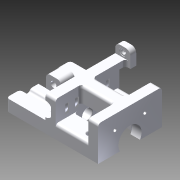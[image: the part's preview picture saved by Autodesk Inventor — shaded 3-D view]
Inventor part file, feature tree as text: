
AUTODESK INVENTOR PART (.ipt)
format: ipt  version: 2015 SP1 (Build 190203100, 203)  size: 731,136 bytes
history: native  units: mm
features: sketch x30, extrude x26, fillet x15, projected_geometry x14, reference x8, hole x4, mirror x1, plane x1, other x1, revolve x1
ambient origin geometry x8: Origin, YZ Plane, XZ Plane, XY Plane, X Axis, Y Axis, Z Axis, Center Point
bodies: Solid1 (feature_tree)
feature tree (101):
  extrude  "Extrusion1"  Depth=12.0mm
  extrude  "Extrusion2"  Depth=10.0mm
  extrude  "Extrusion3"  Depth=25.0mm TaperAngle=0.0deg
  extrude  "Extrusion4"  Depth=16.0mm TaperAngle=0.0deg
  extrude  "Extrusion5"  Depth=24.0mm TaperAngle=0.0deg
  extrude  "Extrusion6"  Depth=2.0mm
  extrude  "Extrusion7"  Depth=4.0mm
  mirror  "Mirror1"
  plane  "Work Plane1"
  extrude  "Extrusion9"  Depth=4.0mm
  sketch  "Sketch8"  dims[d19=4.0mm d20=4.0mm]
  other  "Work Axis1"
  revolve  "Revolution1"  [1 undecoded]
  fillet  "Fillet9"  Radius=2.0mm
  fillet  "Fillet11"  Radius=1.75mm
  extrude  "Extrusion18"  Depth=10.0mm TaperAngle=0.0deg
  extrude  "Extrusion19"  Depth=1.75mm
  extrude  "Extrusion20"  Depth=10.0mm TaperAngle=0.0deg
  fillet  "Fillet13"  Radius=5.0mm
  fillet  "Fillet12"  Radius=5.0mm
  extrude  "Extrusion21"  Depth=1.5mm
  extrude  "Extrusion22"  Depth=10.0mm
  extrude  "Extrusion23"  Depth=22.2mm
  fillet  "Fillet15"  Radius=8.0mm
  fillet  "Fillet16"  Radius=10.5mm
  fillet  "Fillet17"  Radius=8.0mm
  fillet  "Fillet18"  Radius=2.0mm
  hole  "Hole1"  [1 undecoded]
  extrude  "Extrusion25"  Depth=15.5mm
  extrude  "Extrusion26"  Depth=3.0mm TaperAngle=0.0deg
  fillet  "Fillet19"  Radius=2.0mm
  fillet  "Fillet20"  Radius=3.0mm
  hole  "Hole2"  [1 undecoded]
  hole  "Hole3"  [1 undecoded]
  fillet  "Fillet21"  Radius=19.0mm
  extrude  "Extrusion27"  Depth=14.0mm
  extrude  "Extrusion28"  Depth=16.0mm
  fillet  "Fillet23"  Radius=14.0mm
  extrude  "Extrusion29"  Depth=10.0mm TaperAngle=0.0deg
  extrude  "Extrusion30"  Depth=3.0mm
  hole  "Hole4"  [1 undecoded]
  extrude  "Extrusion31"  Depth=3.0mm
  fillet  "Fillet24"  Radius=4.5mm
  fillet  "Fillet25"  Radius=6.3515mm
  extrude  "Extrusion32"  Depth=3.0mm
  extrude  "Extrusion33"  TaperAngle=0.0deg  [1 undecoded]
  extrude  "Extrusion34"  Depth=10.0mm TaperAngle=0.0deg
  fillet  "Fillet26"  Radius=4.0mm
  extrude  "Extrusion35"  Depth=10.0mm
  extrude  "Extrusion36"  Depth=10.0mm TaperAngle=0.0deg
  sketch  "Sketch1"  dims[d0=66.0mm d1=12.0mm]
  sketch  "Sketch2"  dims[d2=10.0mm d3=0.0mm d4=14.0mm]
  sketch  "Sketch3"  dims[d5=14.0mm d6=25.0mm d7=0.0mm]
  reference  "Reference1"
  reference  "Reference2"
  sketch  "Sketch4"  dims[d8=25.0mm d9=0.0mm d10=16.0mm d11=0.0mm]
  projected_geometry  "Projected Loop1"
  sketch  "Sketch6"  dims[d13=10.5mm d14=24.0mm d15=0.0mm]
  sketch  "Sketch7"  dims[d16=20.0mm d17=0.0mm d18=2.0mm]
  reference  "Reference4"
  sketch  "Sketch9"  dims[d21=4.0mm d22=4.0mm]
  sketch  "Sketch11"  dims[d23=6.0mm d24=6.0mm d25=2.0mm d26=1.75mm]
  sketch  "Sketch17"  dims[d27=10.0mm d28=5.0mm d29=0.0mm]
  sketch  "Sketch20"  dims[d30=-29.0mm d35=1.75mm]
  sketch  "Sketch21"  dims[d36=10.0mm d37=8.0mm d38=0.0mm d39=5.0mm d40=5.0mm]
  projected_geometry  "Projected Loop3"
  sketch  "Sketch22"  dims[d41=90.0deg d71=1.5mm]
  projected_geometry  "Projected Loop4"
  projected_geometry  "Projected Loop5"
  sketch  "Sketch23"  dims[d73=3.0mm d76=10.0mm]
  projected_geometry  "Projected Loop6"
  sketch  "Sketch25"  dims[d84=18.0mm d85=0.0mm d86=22.2mm d87=8.0mm d88=0.0mm d89=10.5mm d90=8.0mm d91=0.0mm d92=2.0mm]
  projected_geometry  "Projected Loop8"
  sketch  "Sketch27"  dims[d93=0.75mm d94=18.0mm d95=0.0mm]
  reference  "Reference8"
  sketch  "Sketch28"  dims[d97=18.0mm d98=0.0mm d99=15.5mm]
  projected_geometry  "Projected Loop9"
  reference  "Reference9"
  sketch  "Sketch29"  dims[d100=14.0mm d101=17.0mm d102=0.0mm d106=2.0mm d107=3.0mm]
  projected_geometry  "Projected Loop10"
  sketch  "Sketch31"  dims[d108=4.0mm d109=10.0mm]
  reference  "Reference12"
  reference  "Reference13"
  sketch  "Sketch32"  dims[d110=6.0mm d111=6.0mm d112=4.0mm d113=2.0mm d114=90.0deg d115=8.0mm d116=20.594885mm d117=14.0mm d118=19.0mm]
  sketch  "Sketch33"  dims[d119=24.0mm d120=14.0mm]
  projected_geometry  "Projected Loop11"
  sketch  "Sketch34"  dims[d121=19.0mm d122=16.0mm d123=14.0mm]
  projected_geometry  "Projected Loop12"
  sketch  "Sketch35"  dims[d124=44.0mm d125=0.0mm d126=10.0mm d127=0.0mm]
  projected_geometry  "Projected Loop13"
  sketch  "Sketch36"  dims[d128=3.0mm d129=3.0mm]
  sketch  "Sketch37"  dims[d130=3.2mm d131=6.0mm d132=6.0mm d133=4.0mm d134=90.0deg d135=8.0mm d136=20.594885mm d137=1.0mm]
  sketch  "Sketch38"  dims[d138=3.2mm d139=6.0mm d140=6.0mm d141=3.0mm d142=90.0deg d143=8.0mm d144=20.594885mm d145=7.9mm d146=4.5mm d147=0.0mm d148=6.3515mm]
  sketch  "Sketch39"  dims[d149=6.2mm d150=0.0mm d152=3.0mm]
  projected_geometry  "Projected Loop14"
  sketch  "Sketch40"  dims[d153=15.75mm d154=0.0mm]
  projected_geometry  "Projected Loop15"
  sketch  "Sketch42"  dims[d155=6.0mm d156=0.0mm d157=10.0mm d158=0.0mm d159=4.0mm]
  projected_geometry  "Projected Loop17"
  sketch  "Sketch43"  dims[d160=5.0mm d161=6.0mm d162=4.0mm d163=2.0mm d164=90.0deg d165=8.0mm d166=20.594885mm d167=7.1mm d168=3.2mm d169=0.0mm d170=5.0mm d171=3.0mm d172=7.5mm d173=0.5mm d174=0.0mm d175=2.0mm d176=1.0mm d177=0.0mm d178=1.0mm d179=0.0mm d181=0.4mm d182=0.4mm d183=10.0mm d184=0.0mm d185=1.0mm d186=10.0mm d187=0.0mm]
  reference  "Reference14"
note: 6 required parameter values undecoded (feature->parameter linkage not recoverable at this tier; creation-order binding heuristic only, values carry confidence <= 0.55)